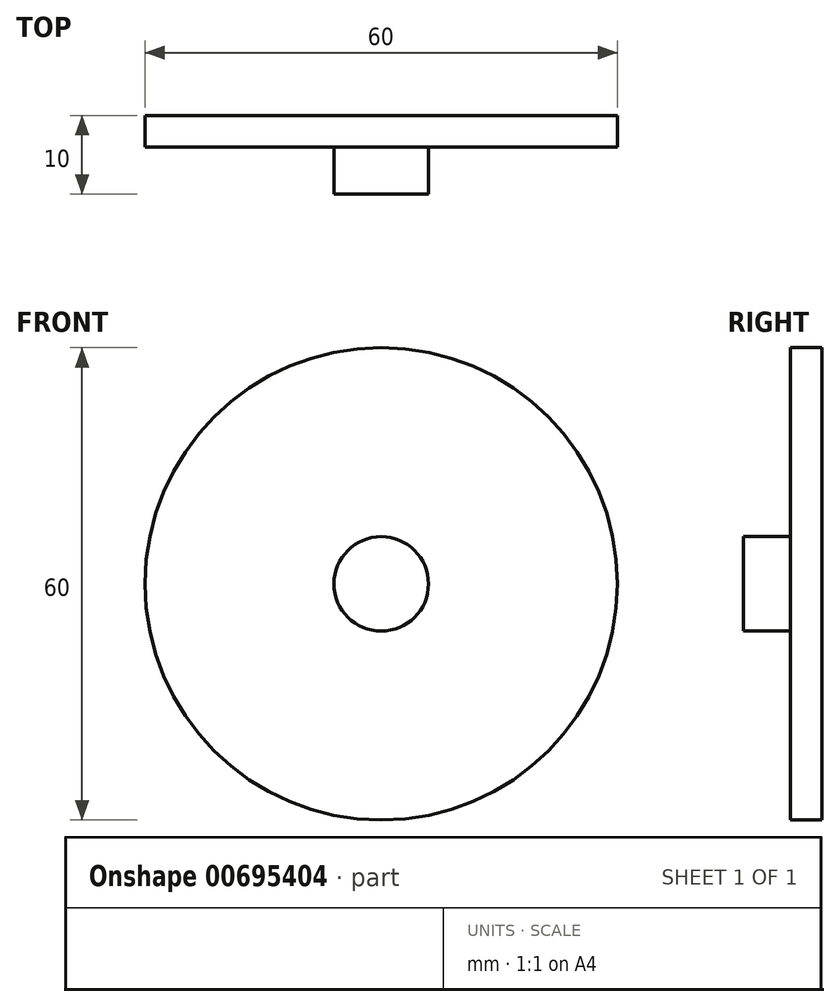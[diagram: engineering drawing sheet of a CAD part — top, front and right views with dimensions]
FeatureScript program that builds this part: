
annotation { "Feature Type Name" : "Feature", "Feature Type Description" : "" }
export const myFeature = defineFeature(function(context is Context, id is Id, definition is map)
    precondition{}
    {
        {
            var Q0;
            Q0=qCreatedBy(makeId("Front.planeOp"),FACE);
            var sketch = newSketch(context, id + "F0", { "sketchPlane" : qUnion([Q0])});
            skCircle(sketch, "E0", {"center": v(0, 0) * mm, "radius": 30 * mm});
            skSolve(sketch);
        }
        {
            var Q0;
            Q0=qSketchRegion(id+"F0",true);
            extrude(context, id + "F1", {"entities" : qUnion([Q0]), "depth" : 4 * mm, "offsetDistance" : 25 * mm});
        }
        {
            var Q0;
            Q0=qCreatedBy(makeId("Front.planeOp"),FACE);
            var sketch = newSketch(context, id + "F2", { "sketchPlane" : qUnion([Q0])});
            skCircle(sketch, "E1", {"center": v(0, 0) * mm, "radius": 6 * mm});
            skSolve(sketch);
        }
        {
            var Q0;
            Q0=qSketchRegion(id+"F2",true);
            extrude(context, id + "F3", {"entities" : qUnion([Q0]), "operationType" : NewBodyOperationType.ADD, "depth" : 10 * mm, "offsetDistance" : 25 * mm});
        }
    });
